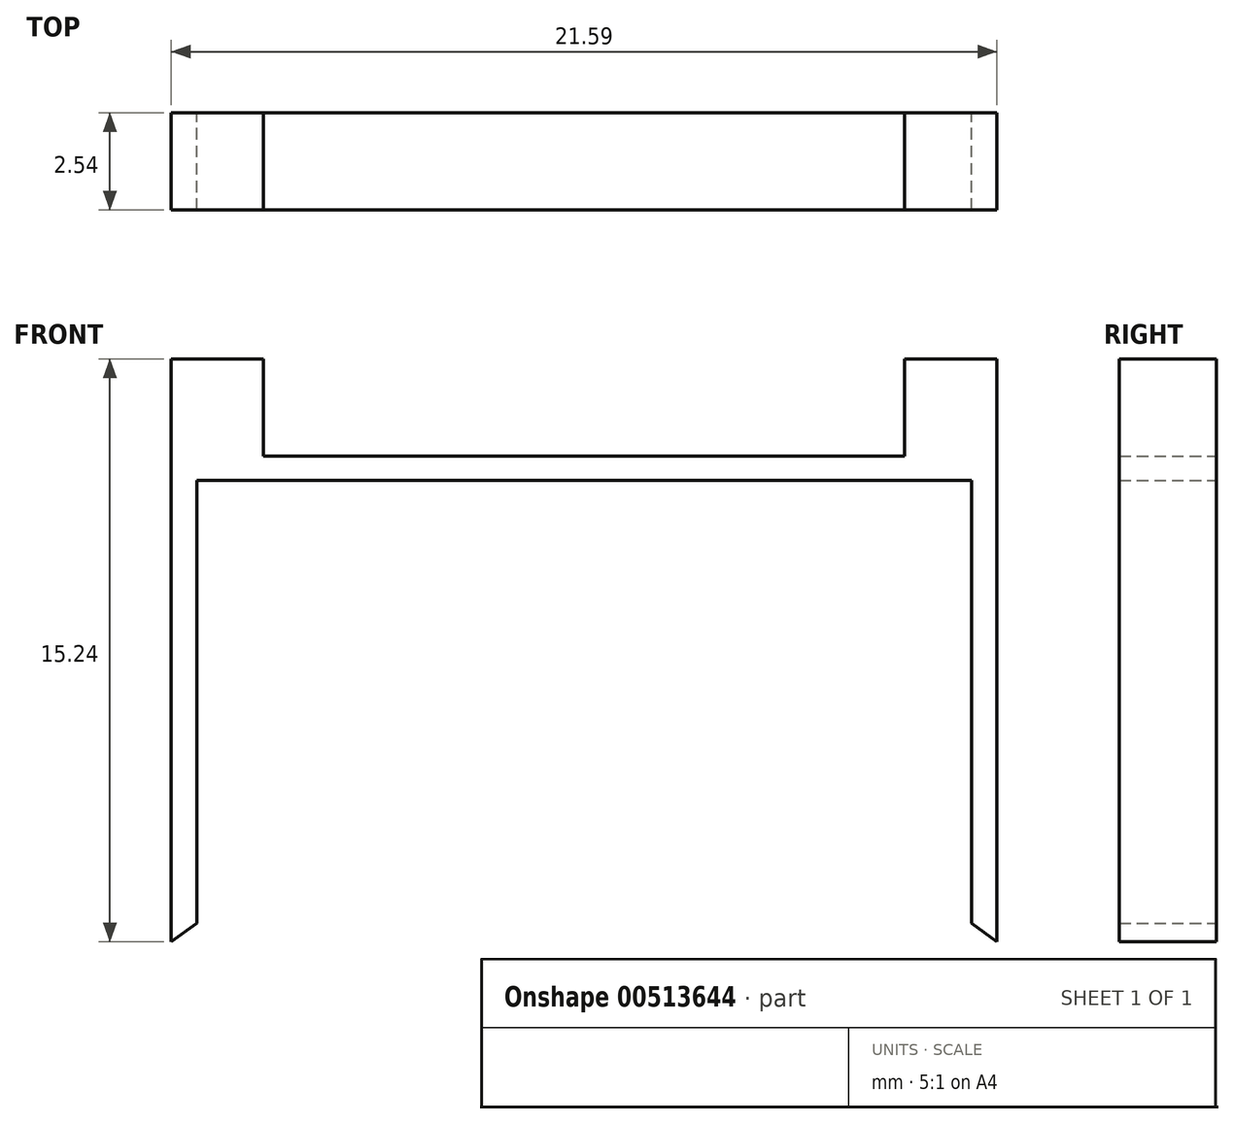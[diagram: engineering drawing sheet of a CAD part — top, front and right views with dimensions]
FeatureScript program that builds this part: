
annotation { "Feature Type Name" : "Feature", "Feature Type Description" : "" }
export const myFeature = defineFeature(function(context is Context, id is Id, definition is map)
    precondition{}
    {
        {
            var Q0;
            Q0=qCreatedBy(makeId("Front.planeOp"),FACE);
            var sketch = newSketch(context, id + "F0", { "sketchPlane" : qUnion([Q0])});
            skLineSegment(sketch, "E0", {"start": v(-46.91, 19.13) * mm, "end": v(-46.91, 6.43) * mm});
            skLineSegment(sketch, "E1", {"start": v(-25.32, 6.43) * mm, "end": v(-25.32, 19.13) * mm});
            skLineSegment(sketch, "E2", {"start": v(-46.91, 19.13) * mm, "end": v(-25.32, 19.13) * mm});
            skPoint(sketch, "E3.end.orphan", {"position": v(-41.14, 19.13) * mm});
            skPoint(sketch, "E4.start.orphan", {"position": v(-41.14, 14.28) * mm});
            skLineSegment(sketch, "E5", {"start": v(-46.91, 19.13) * mm, "end": v(-46.91, 21.67) * mm});
            skLineSegment(sketch, "E6", {"start": v(-46.91, 21.67) * mm, "end": v(-44.5, 21.67) * mm});
            skLineSegment(sketch, "E7", {"start": v(-44.5, 21.67) * mm, "end": v(-44.5, 19.13) * mm});
            skLineSegment(sketch, "E8", {"start": v(-25.32, 19.13) * mm, "end": v(-25.32, 21.67) * mm});
            skLineSegment(sketch, "E9", {"start": v(-25.32, 21.67) * mm, "end": v(-27.73, 21.67) * mm});
            skLineSegment(sketch, "E10", {"start": v(-27.73, 21.67) * mm, "end": v(-27.73, 19.13) * mm});
            skLineSegment(sketch, "E11.top", {"start": v(-46.24, 18.5) * mm, "end": v(-25.99, 18.5) * mm});
            skLineSegment(sketch, "E11.left", {"start": v(-46.24, 6.92) * mm, "end": v(-46.24, 18.5) * mm});
            skLineSegment(sketch, "E11.right", {"start": v(-25.99, 6.92) * mm, "end": v(-25.99, 18.5) * mm});
            skLineSegment(sketch, "E12", {"start": v(-46.91, 6.43) * mm, "end": v(-46.24, 6.92) * mm});
            skLineSegment(sketch, "E13", {"start": v(-25.99, 6.92) * mm, "end": v(-25.32, 6.43) * mm});
            skSolve(sketch);
        }
        {
            var Q0;
            {var subQ1=sQuery(id+"F0.wireOp",EDGE,"E0");Q0=makeQuery(id+"F0.imprint","IMPRINT",FACE,{"disambiguationData":[TD([[makeQuery(id+"F0.imprint","IMPRINT",EDGE,{"derivedFrom":subQ1}),1.0]])]});}
            var Q1;
            {var subQ0=sQuery(id+"F0.wireOp",EDGE,"E5");Q1=makeQuery(id+"F0.imprint","IMPRINT",FACE,{"disambiguationData":[TD([[makeQuery(id+"F0.imprint","IMPRINT",EDGE,{"derivedFrom":subQ0}),-1.0]])]});}
            var Q2;
            {var subQ0=sQuery(id+"F0.wireOp",EDGE,"E8");Q2=makeQuery(id+"F0.imprint","IMPRINT",FACE,{"disambiguationData":[TD([[makeQuery(id+"F0.imprint","IMPRINT",EDGE,{"derivedFrom":subQ0}),1.0]])]});}
            extrude(context, id + "F1", {"entities" : qUnion([Q0, Q1, Q2]), "depth" : 2.54 * mm, "offsetDistance" : 25.4 * mm});
        }
    });
